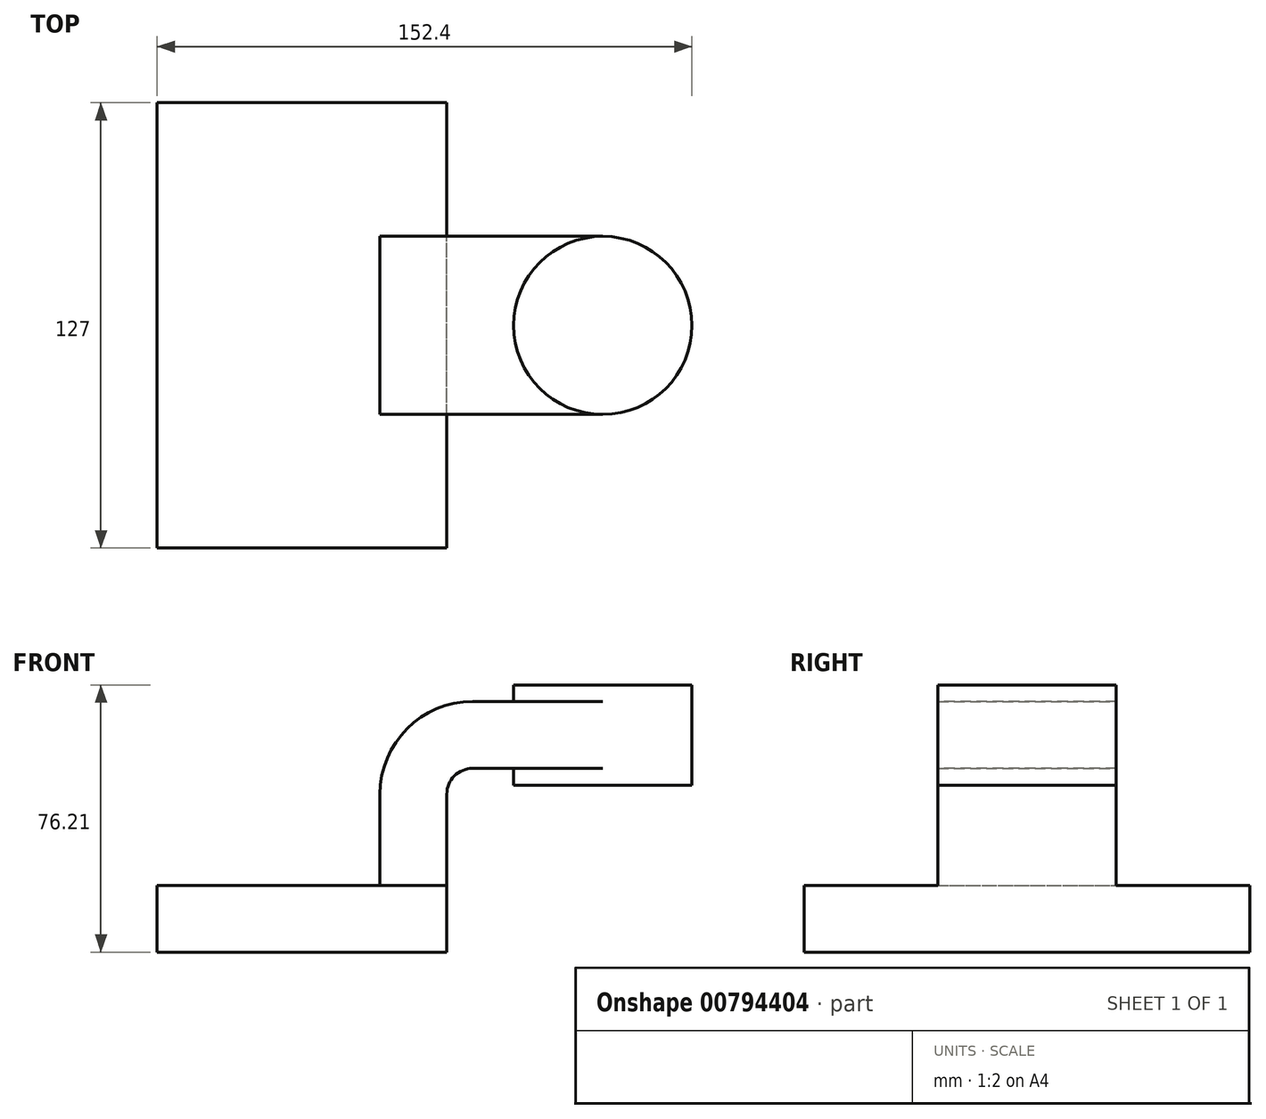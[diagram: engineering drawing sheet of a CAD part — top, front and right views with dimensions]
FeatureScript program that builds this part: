
annotation { "Feature Type Name" : "Feature", "Feature Type Description" : "" }
export const myFeature = defineFeature(function(context is Context, id is Id, definition is map)
    precondition{}
    {
        {
            var Q0;
            Q0=qCreatedBy(makeId("Front.planeOp"),FACE);
            var sketch = newSketch(context, id + "F0", { "sketchPlane" : qUnion([Q0])});
            skLineSegment(sketch, "E0.bottom", {"start": v(41.28, -9.52) * mm, "end": v(-41.28, -9.53) * mm});
            skLineSegment(sketch, "E0.top", {"start": v(41.28, 9.53) * mm, "end": v(-41.28, 9.52) * mm});
            skLineSegment(sketch, "E0.left", {"start": v(41.28, -9.52) * mm, "end": v(41.28, 9.53) * mm});
            skLineSegment(sketch, "E0.right", {"start": v(-41.28, -9.53) * mm, "end": v(-41.28, 9.52) * mm});
            skPoint(sketch, "E0.middle", {"position": v(0, 0) * mm});
            skLineSegment(sketch, "E1.bottom", {"start": v(60.32, 38.1) * mm, "end": v(111.12, 38.1) * mm});
            skLineSegment(sketch, "E1.top", {"start": v(60.32, 66.68) * mm, "end": v(111.12, 66.68) * mm});
            skLineSegment(sketch, "E1.left", {"start": v(60.32, 38.1) * mm, "end": v(60.32, 66.67) * mm});
            skLineSegment(sketch, "E1.right", {"start": v(111.12, 38.1) * mm, "end": v(111.12, 66.68) * mm});
            skPoint(sketch, "E1.middle", {"position": v(85.72, 52.39) * mm});
            skLineSegment(sketch, "E2", {"start": v(41.28, 9.53) * mm, "end": v(41.28, 35.5) * mm});
            skArc(sketch, "E3", {"start": v(41.28, 35.5) * mm, "mid": v(43.43, 40.72) * mm, "end": v(48.64, 42.88) * mm});
            skArc(sketch, "E4.1", {"start": v(22.22, 35.5) * mm, "mid": v(29.96, 54.19) * mm, "end": v(48.64, 61.93) * mm});
            skLineSegment(sketch, "E4.2", {"start": v(22.22, 9.53) * mm, "end": v(22.22, 35.5) * mm});
            skPoint(sketch, "E5.endSnap0", {"position": v(85.72, 66.68) * mm});
            skFitSpline(sketch, "E6", {"points": [v(-41.28, 9.52) * mm, v(48.64, 61.93) * mm], "startDerivative": vector(5.35, 78.21) * mm, "endDerivative": vector(96.7, -0.97) * mm});
            skLineSegment(sketch, "E7", {"start": v(85.72, 66.68) * mm, "end": v(85.72, 38.1) * mm});
            skLineSegment(sketch, "E8", {"start": v(48.64, 61.93) * mm, "end": v(85.72, 61.93) * mm});
            skLineSegment(sketch, "E9", {"start": v(48.64, 42.88) * mm, "end": v(85.72, 42.88) * mm});
            skSolve(sketch);
        }
        {
            var Q0;
            Q0=makeQuery(id+"F0.imprint","IMPRINT",FACE,{"disambiguationData":[TD([[makeQuery(id+"F0.imprint","IMPRINT",EDGE,{"derivedFrom":sQuery(id+"F0.wireOp",EDGE,"E0.bottom")}),-1.0]])]});
            extrude(context, id + "F1", {"entities" : qUnion([Q0]), "endBound" : BoundingType.SYMMETRIC, "depth" : 127 * mm, "offsetDistance" : 25.4 * mm});
        }
        {
            var Q0;
            {var subQ0=sQuery(id+"F0.wireOp",EDGE,"E9");var subQ1=sQuery(id+"F0.wireOp",EDGE,"E1.left");var subQ2=makeQuery(id+"F0.imprint","INTERSECT",VERTEX,{"derivedFrom":[subQ1,subQ0]});Q0=makeQuery(id+"F0.imprint","IMPRINT",FACE,{"disambiguationData":[TD([[makeQuery(id+"F0.imprint","IMPRINT",EDGE,{"disambiguationData":[TD([[subQ2,-1.0]])],"derivedFrom":subQ1}),-1.0]])]});}
            var Q1;
            {var subQ1=sQuery(id+"F0.wireOp",EDGE,"E2");Q1=makeQuery(id+"F0.imprint","IMPRINT",FACE,{"disambiguationData":[TD([[makeQuery(id+"F0.imprint","IMPRINT",EDGE,{"derivedFrom":subQ1}),1.0]])]});}
            extrude(context, id + "F2", {"entities" : qUnion([Q0, Q1]), "operationType" : NewBodyOperationType.ADD, "endBound" : BoundingType.SYMMETRIC, "depth" : 50.8 * mm, "offsetDistance" : 25.4 * mm});
        }
        {
            var Q0;
            Q0=makeQuery(id+"F0.imprint","IMPRINT",FACE,{"disambiguationData":[TD([[makeQuery(id+"F0.imprint","IMPRINT",EDGE,{"derivedFrom":sQuery(id+"F0.wireOp",EDGE,"E4.1")}),1.0]])]});
            extrude(context, id + "F3", {"entities" : qUnion([Q0]), "operationType" : NewBodyOperationType.ADD, "endBound" : BoundingType.SYMMETRIC, "depth" : 15.88 * mm, "offsetDistance" : 25.4 * mm});
        }
        {
            var Q0;
            {var subQ0=sQuery(id+"F0.wireOp",EDGE,"E1.right");Q0=makeQuery(id+"F0.imprint","IMPRINT",FACE,{"disambiguationData":[TD([[makeQuery(id+"F0.imprint","IMPRINT",EDGE,{"derivedFrom":subQ0}),1.0]])]});}
            var Q1;
            Q1=sQuery(id+"F0.wireOp",EDGE,"E7");
            revolve(context, id + "F4", {"operationType" : NewBodyOperationType.ADD, "surfaceOperationType" : NewSurfaceOperationType.NEW, "entities" : qUnion([Q0]), "axis" : qUnion([Q1]), "revolveType" : RevolveType.FULL});
        }
    });
